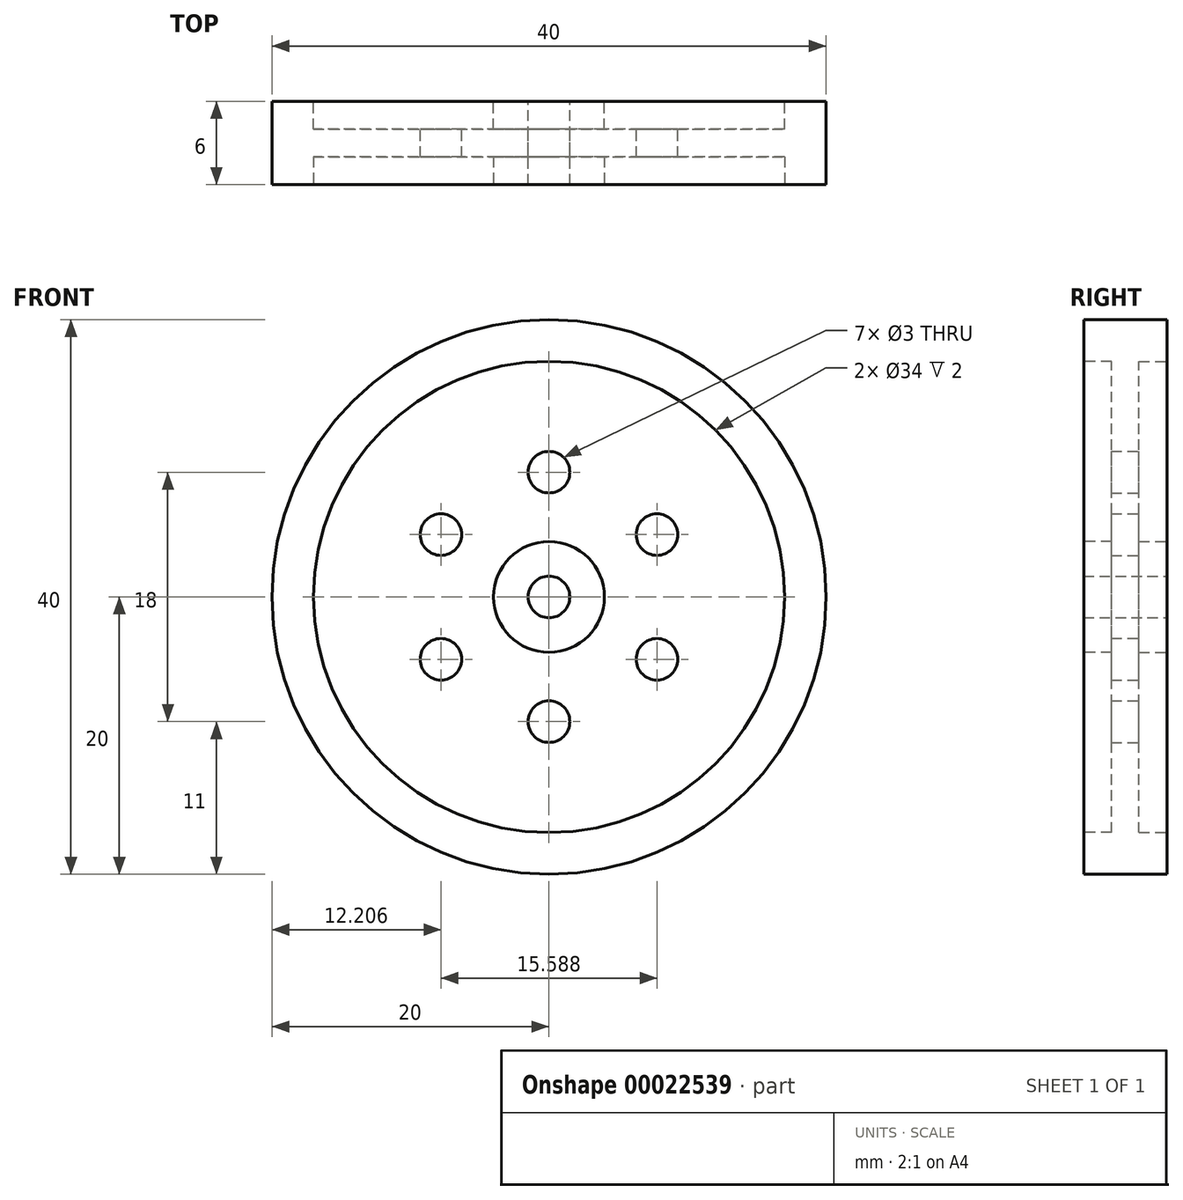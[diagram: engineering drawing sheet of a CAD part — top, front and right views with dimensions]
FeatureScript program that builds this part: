
annotation { "Feature Type Name" : "Feature", "Feature Type Description" : "" }
export const myFeature = defineFeature(function(context is Context, id is Id, definition is map)
    precondition{}
    {
        {
            var Q0;
            Q0=qCreatedBy(makeId("Front.planeOp"),FACE);
            var sketch = newSketch(context, id + "F0", { "sketchPlane" : qUnion([Q0])});
            skCircle(sketch, "E0", {"center": v(0, 0) * mm, "radius": 20 * mm});
            skCircle(sketch, "E1", {"center": v(0, 0) * mm, "radius": 17 * mm});
            skCircle(sketch, "E2", {"center": v(0, 0) * mm, "radius": 1.5 * mm});
            skCircle(sketch, "E3", {"center": v(0, 0) * mm, "radius": 4 * mm});
            skLineSegment(sketch, "E4", {"start": v(0, 0) * mm, "end": v(0, 9) * mm});
            skCircle(sketch, "E5", {"center": v(0, 9) * mm, "radius": 1.5 * mm});
            skCircle(sketch, "E6.1.0", {"center": v(-7.8, 4.5) * mm, "radius": 1.5 * mm});
            skCircle(sketch, "E6.2.0", {"center": v(-7.8, -4.5) * mm, "radius": 1.5 * mm});
            skCircle(sketch, "E6.3.0", {"center": v(0, -9) * mm, "radius": 1.5 * mm});
            skCircle(sketch, "E6.4.0", {"center": v(7.8, -4.5) * mm, "radius": 1.5 * mm});
            skCircle(sketch, "E6.5.0", {"center": v(7.8, 4.5) * mm, "radius": 1.5 * mm});
            skSolve(sketch);
        }
        {
            var Q0;
            Q0=makeQuery(id+"F0.imprint","IMPRINT",FACE,{"disambiguationData":[TD([[makeQuery(id+"F0.imprint","IMPRINT",EDGE,{"derivedFrom":sQuery(id+"F0.wireOp",EDGE,"E0")}),1.0]])]});
            var Q1;
            Q1=makeQuery(id+"F0.imprint","IMPRINT",FACE,{"disambiguationData":[TD([[makeQuery(id+"F0.imprint","IMPRINT",EDGE,{"derivedFrom":sQuery(id+"F0.wireOp",EDGE,"E1")}),1.0]])]});
            var Q2;
            Q2=makeQuery(id+"F0.imprint","IMPRINT",FACE,{"disambiguationData":[TD([[makeQuery(id+"F0.imprint","IMPRINT",EDGE,{"derivedFrom":sQuery(id+"F0.wireOp",EDGE,"E2")}),-1.0]])]});
            extrude(context, id + "F1", {"entities" : qUnion([Q0, Q1, Q2]), "depth" : 6 * mm});
        }
        {
            var Q0;
            Q0=makeQuery(id+"F0.imprint","IMPRINT",FACE,{"disambiguationData":[TD([[makeQuery(id+"F0.imprint","IMPRINT",EDGE,{"derivedFrom":sQuery(id+"F0.wireOp",EDGE,"E1")}),1.0]])]});
            extrude(context, id + "F2", {"entities" : qUnion([Q0]), "operationType" : NewBodyOperationType.REMOVE, "depth" : 2 * mm});
        }
        {
            var Q0;
            Q0=makeQuery(id+"F1.opExtrude","CAP_FACE",FACE,{"disambiguationData":[OSD([sQuery(id+"F0.wireOp",EDGE,"E0"),sQuery(id+"F0.wireOp",EDGE,"E2"),sQuery(id+"F0.wireOp",EDGE,"E5"),sQuery(id+"F0.wireOp",EDGE,"E6.1.0"),sQuery(id+"F0.wireOp",EDGE,"E6.2.0"),sQuery(id+"F0.wireOp",EDGE,"E6.3.0"),sQuery(id+"F0.wireOp",EDGE,"E6.4.0"),sQuery(id+"F0.wireOp",EDGE,"E6.5.0")])],"isStart":false});
            var sketch = newSketch(context, id + "F3", { "sketchPlane" : qUnion([Q0])});
            skCircle(sketch, "E7", {"center": v(0, 0) * mm, "radius": 17 * mm});
            skCircle(sketch, "E8", {"center": v(0, 0) * mm, "radius": 4 * mm});
            skCircle(sketch, "E9", {"center": v(0, 0) * mm, "radius": 1.5 * mm});
            skSolve(sketch);
        }
        {
            var Q0;
            Q0=makeQuery(id+"F3.imprint","IMPRINT",FACE,{"disambiguationData":[TD([[makeQuery(id+"F3.imprint","IMPRINT",EDGE,{"derivedFrom":sQuery(id+"F3.wireOp",EDGE,"E7")}),1.0]])]});
            extrude(context, id + "F4", {"entities" : qUnion([Q0]), "operationType" : NewBodyOperationType.REMOVE, "oppositeDirection" : true, "depth" : 2 * mm});
        }
    });
